# Revit family: Plumbing-Flushometer-Sloan-Valve-ROYAL-195 ESS TMO SBX_
name_source: partatom
category: Plumbing Fixtures
units: mm (PartAtom-declared; Revit-internal decimal feet)

## family parameters
Cut with Voids When Loaded = Yes
Host = Face
OmniClass Number = 23.45.05.14.99
OmniClass Title = Other Sanitary Washing Plumbing Fixtures
Part Type = Normal
Room Calculation Point = No
Round Connector Dimension = Use Diameter
Shared = No

## types (4) — shared parameters
Apparent Load = 0 VA
Assembly Code = D2020300
CW Connection = Yes
Centerline of Supply from Top of Fixture = 13 1/2"
Centerline of Supply to Centerline of Valve = 4 3/4"
Connector Description = Electrical Connection
Current = 0 A
Default Elevation = 0"
Edition number = 1
Flushometer Material = Sloan Valve - Finish - Rough Brass
HW Connection = No
Keynote = 15410
Manufacturer = Sloan Valve
Number of Poles = 1
Operating Water Pressure = 15 – 80 PSI (103 – 552 kPa)
Power Factor = 1
Product Material = Sloan Valve - Finish - Rough Brass
Product data url = https://bimobject.com
URL = www.sloanvalve.com
Valve Pressure Drop = 0.00 psi
Vent Connection = No
Voltage = 24 V
Waste Connection = No
Water Inlet Connection Description = Water Inlet Connection
Water Inlet Connection Diameter = 1"
zero-valued in all types: CWFU, HWFU, WFU

## per-type parameters (varying)
| type | Description | Flush Rate | Part Number |
| ROYAL 195 IR TMO SBX-0.125-DBP-TMO-2-10-3/4-LDIM-HW-LT-10-1/2-VB-24V | 0.125 gpf, Dual-Filtered Bypass, Rough Brass Finish, 0.75 Flush Connection, Fixture Connection , Single Flush, 0.75" Inlet, 3/4" Control Stop, 2-10.75 L Dimension, True Mechanical Override, Hardwired, Infrared, 10.5" Vacuum Breaker, 24V, Royal® Concealed Sensor Urinal Hydraulic Flushometer. | 0.125 gpf (0.5 Lpf) | 34532004 |
| ROYAL 195 IR TMO SBX-0.25-DBP-TMO-2-10-3/4-LDIM-HW-LT-10-1/2-VB-24V | 0.25 gpf, Dual-Filtered Bypass, Rough Brass Finish, 0.75 Flush Connection, Fixture Connection , Single Flush, 0.75" Inlet, 3/4" Control Stop, 2-10.75 L Dimension, True Mechanical Override, Hardwired, Infrared, 10.5" Vacuum Breaker, 24V, Royal® Concealed Sensor Urinal Hydraulic Flushometer. | 0.25 gpf (0.9 Lpf) | 34532003 |
| ROYAL 195 IR TMO SBX-0.5-DBP-TMO-2-10-3/4-LDIM-HW-LT-10-1/2-VB-24V | 0.5 gpf, Dual-Filtered Bypass, Rough Brass Finish, 0.75 Flush Connection, Fixture Connection , Single Flush, 0.75" Inlet, 3/4" Control Stop, 2-10.75 L Dimension, True Mechanical Override, Hardwired,Infrared, 10.5" Vacuum Breaker, 24V, Royal® Concealed Sensor Urinal Hydraulic Flushometer. | 0.5 gpf (1.9 Lpf) | 34532002 |
| ROYAL 195 IR TMO SBX-1.0-DBP-TMO-2-10-3/4-LDIM-HW-LT-10-1/2-VB-24V | 1.0 gpf, Dual-Filtered Bypass, Rough Brass Finish, 0.75 Flush Connection, Fixture Connection , Single Flush, 0.75" Inlet, 3/4" Control Stop, 2-10.75 L Dimension, True Mechanical Override, Hardwired,Infrared, 10.5" Vacuum Breaker, 24V, Royal® Concealed Sensor Urinal Hydraulic Flushometer. | 1.0 gpf (3.8 Lpf) | 34532001 |

note: column(s) folded — value = type name in every type: Model

## geometry (parser evidence)
native form markers: Sweep x2
no freeform markers — native parametric forms only
